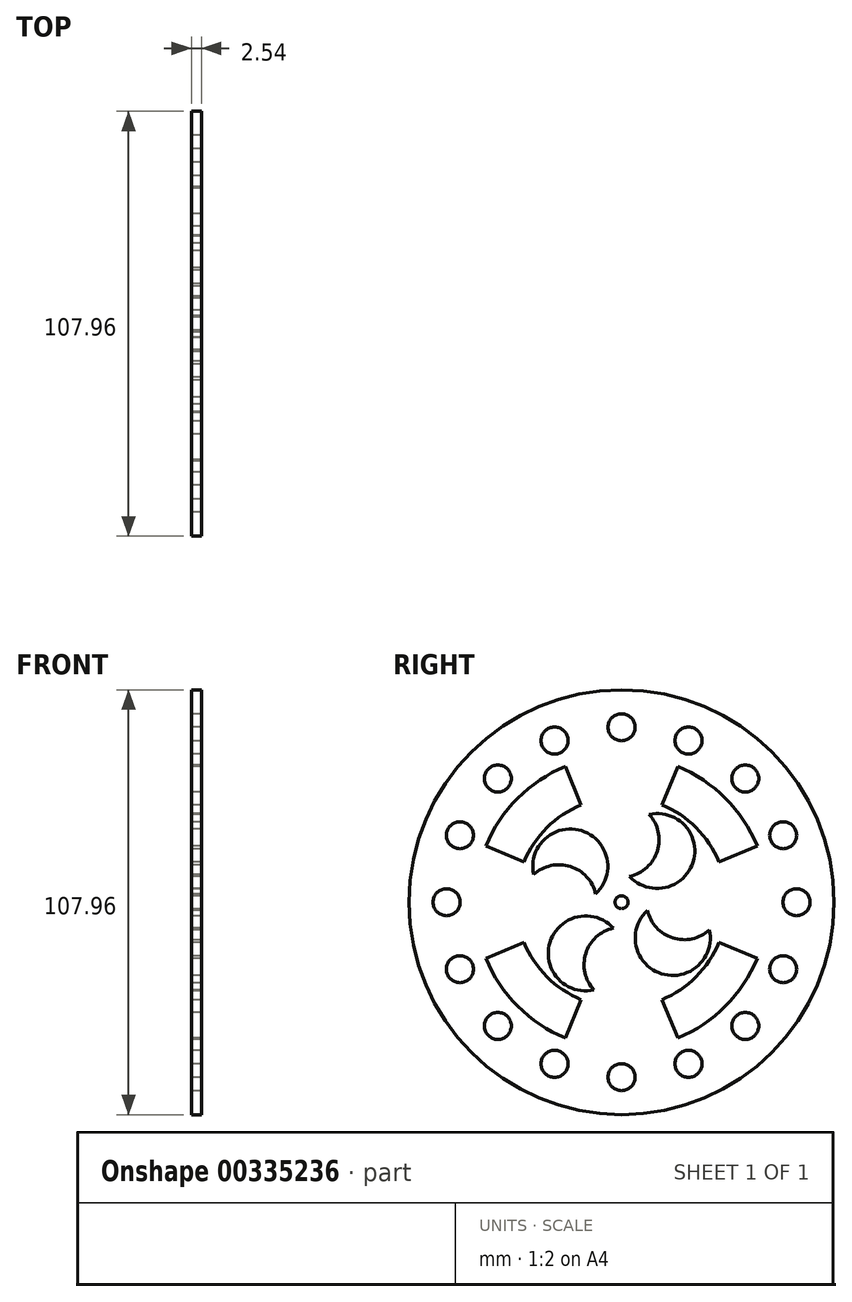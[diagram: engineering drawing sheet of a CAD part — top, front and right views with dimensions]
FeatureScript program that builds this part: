
annotation { "Feature Type Name" : "Feature", "Feature Type Description" : "" }
export const myFeature = defineFeature(function(context is Context, id is Id, definition is map)
    precondition{}
    {
        {
            var Q0;
            Q0=qCreatedBy(makeId("Right.planeOp"),FACE);
            var sketch = newSketch(context, id + "F0", { "sketchPlane" : qUnion([Q0])});
            skCircle(sketch, "E0", {"center": v(0, 0) * mm, "radius": 53.98 * mm});
            skCircle(sketch, "E1", {"center": v(0, 0) * mm, "radius": 1.65 * mm});
            skCircle(sketch, "E2", {"center": v(0, 44.45) * mm, "radius": 3.43 * mm});
            skCircle(sketch, "E3", {"center": v(-44.45, 0) * mm, "radius": 3.43 * mm});
            skLineSegment(sketch, "E4", {"start": v(-76.85, 0) * mm, "end": v(-47.88, 0) * mm, "construction": true});
            skArc(sketch, "E5", {"start": v(2.07, 6.58) * mm, "mid": v(9.09, 13.02) * mm, "end": v(7.02, 22.32) * mm});
            skArc(sketch, "E6", {"start": v(6.58, -2.07) * mm, "mid": v(13.02, -9.09) * mm, "end": v(22.32, -7.02) * mm});
            skArc(sketch, "E7", {"start": v(6.58, -2.07) * mm, "mid": v(10.16, -18.17) * mm, "end": v(22.32, -7.02) * mm});
            skArc(sketch, "E8.trimOffspring", {"start": v(-6.58, 2.07) * mm, "mid": v(-10.16, 18.17) * mm, "end": v(-22.32, 7.02) * mm});
            skArc(sketch, "E9.trimOffspring", {"start": v(-6.58, 2.07) * mm, "mid": v(-13.02, 9.09) * mm, "end": v(-22.32, 7.02) * mm});
            skArc(sketch, "E10.trimOffspring", {"start": v(-2.07, -6.58) * mm, "mid": v(-18.17, -10.16) * mm, "end": v(-7.02, -22.32) * mm});
            skArc(sketch, "E11.trimOffspring", {"start": v(-2.07, -6.58) * mm, "mid": v(-9.09, -13.02) * mm, "end": v(-7.02, -22.32) * mm});
            skArc(sketch, "E12.trimOffspring", {"start": v(2.07, 6.58) * mm, "mid": v(18.17, 10.16) * mm, "end": v(7.02, 22.32) * mm});
            skLineSegment(sketch, "E13.trimOffspring", {"start": v(-41.02, 0) * mm, "end": v(-1.65, 0) * mm, "construction": true});
            skCircle(sketch, "E14", {"center": v(-31.43, 31.43) * mm, "radius": 3.43 * mm});
            skPoint(sketch, "E15", {"position": v(-37.94, 15.72) * mm});
            skLineSegment(sketch, "E16", {"start": v(-1.53, 0.63) * mm, "end": v(-37.94, 15.72) * mm, "construction": true});
            skLineSegment(sketch, "E17", {"start": v(-37.94, 15.72) * mm, "end": v(-49.87, 20.66) * mm, "construction": true});
            skLineSegment(sketch, "E18", {"start": v(-0.63, 1.53) * mm, "end": v(-15.72, 37.94) * mm, "construction": true});
            skLineSegment(sketch, "E19", {"start": v(-15.72, 37.94) * mm, "end": v(-20.66, 49.87) * mm, "construction": true});
            skCircle(sketch, "E20", {"center": v(-41.07, 17.01) * mm, "radius": 3.43 * mm});
            skCircle(sketch, "E21", {"center": v(-17.01, 41.07) * mm, "radius": 3.43 * mm});
            skLineSegment(sketch, "E22", {"start": v(0, 71.42) * mm, "end": v(0, 1.65) * mm, "construction": true});
            skCircle(sketch, "E23.MirrorC", {"center": v(17.01, 41.07) * mm, "radius": 3.43 * mm});
            skCircle(sketch, "E24.MirrorC", {"center": v(31.43, 31.43) * mm, "radius": 3.43 * mm});
            skCircle(sketch, "E25.MirrorC", {"center": v(41.07, 17.01) * mm, "radius": 3.43 * mm});
            skCircle(sketch, "E26.MirrorC", {"center": v(44.45, 0) * mm, "radius": 3.43 * mm});
            skCircle(sketch, "E27.MirrorC", {"center": v(41.07, -17.01) * mm, "radius": 3.43 * mm});
            skCircle(sketch, "E28.MirrorC", {"center": v(31.43, -31.43) * mm, "radius": 3.43 * mm});
            skCircle(sketch, "E29.MirrorC", {"center": v(17.01, -41.07) * mm, "radius": 3.43 * mm});
            skCircle(sketch, "E30.MirrorC", {"center": v(0, -44.45) * mm, "radius": 3.43 * mm});
            skCircle(sketch, "E31.MirrorC", {"center": v(-17.01, -41.07) * mm, "radius": 3.43 * mm});
            skCircle(sketch, "E32.MirrorC", {"center": v(-31.43, -31.43) * mm, "radius": 3.43 * mm});
            skCircle(sketch, "E33.MirrorC", {"center": v(-41.07, -17.01) * mm, "radius": 3.43 * mm});
            skLineSegment(sketch, "E34.trimOffspring", {"start": v(0, -1.65) * mm, "end": v(0, -67.4) * mm, "construction": true});
            skLineSegment(sketch, "E35.trimOffspring", {"start": v(0, 0) * mm, "end": v(75.85, 0) * mm, "construction": true});
            skLineSegment(sketch, "E36.MirrorCS", {"start": v(0.63, 1.53) * mm, "end": v(15.72, 37.94) * mm, "construction": true});
            skLineSegment(sketch, "E37.MirrorCS", {"start": v(1.53, 0.63) * mm, "end": v(37.94, 15.72) * mm, "construction": true});
            skLineSegment(sketch, "E38.MirrorCS", {"start": v(-1.53, -0.63) * mm, "end": v(-37.94, -15.72) * mm, "construction": true});
            skLineSegment(sketch, "E39.MirrorCS", {"start": v(-0.63, -1.53) * mm, "end": v(-15.72, -37.94) * mm, "construction": true});
            skLineSegment(sketch, "E40.MirrorCS", {"start": v(1.53, -0.63) * mm, "end": v(37.94, -15.72) * mm, "construction": true});
            skLineSegment(sketch, "E41.MirrorCS", {"start": v(0.63, -1.53) * mm, "end": v(15.72, -37.94) * mm, "construction": true});
            skArc(sketch, "E42", {"start": v(-34.49, -14.29) * mm, "mid": v(-26.4, -26.4) * mm, "end": v(-14.29, -34.49) * mm});
            skArc(sketch, "E43", {"start": v(-24.76, -10.25) * mm, "mid": v(-18.95, -18.95) * mm, "end": v(-10.25, -24.76) * mm});
            skLineSegment(sketch, "E44", {"start": v(-24.76, -10.25) * mm, "end": v(-34.49, -14.29) * mm});
            skLineSegment(sketch, "E45", {"start": v(-10.25, -24.76) * mm, "end": v(-14.29, -34.49) * mm});
            skLineSegment(sketch, "E46", {"start": v(24.76, -10.25) * mm, "end": v(34.49, -14.29) * mm});
            skLineSegment(sketch, "E47", {"start": v(10.25, -24.76) * mm, "end": v(14.29, -34.49) * mm});
            skLineSegment(sketch, "E48", {"start": v(24.76, 10.25) * mm, "end": v(34.49, 14.29) * mm});
            skLineSegment(sketch, "E49", {"start": v(10.25, 24.76) * mm, "end": v(14.29, 34.49) * mm});
            skLineSegment(sketch, "E50", {"start": v(-14.29, 34.49) * mm, "end": v(-10.25, 24.76) * mm});
            skLineSegment(sketch, "E51", {"start": v(-34.49, 14.29) * mm, "end": v(-24.76, 10.25) * mm});
            skArc(sketch, "E52.trimOffspring", {"start": v(-14.29, 34.49) * mm, "mid": v(-26.4, 26.4) * mm, "end": v(-34.49, 14.29) * mm});
            skArc(sketch, "E53.trimOffspring", {"start": v(-10.25, 24.76) * mm, "mid": v(-18.95, 18.95) * mm, "end": v(-24.76, 10.25) * mm});
            skArc(sketch, "E54.trimOffspring", {"start": v(24.76, 10.25) * mm, "mid": v(18.95, 18.95) * mm, "end": v(10.25, 24.76) * mm});
            skArc(sketch, "E55.trimOffspring", {"start": v(34.49, 14.29) * mm, "mid": v(26.4, 26.4) * mm, "end": v(14.29, 34.49) * mm});
            skArc(sketch, "E56.trimOffspring", {"start": v(10.25, -24.76) * mm, "mid": v(18.95, -18.95) * mm, "end": v(24.76, -10.25) * mm});
            skArc(sketch, "E57.trimOffspring", {"start": v(14.29, -34.49) * mm, "mid": v(26.4, -26.4) * mm, "end": v(34.49, -14.29) * mm});
            skSolve(sketch);
        }
        {
            var Q0;
            Q0=makeQuery(id+"F0.imprint","IMPRINT",FACE,{"disambiguationData":[TD([[makeQuery(id+"F0.imprint","IMPRINT",EDGE,{"derivedFrom":sQuery(id+"F0.wireOp",EDGE,"E0")}),1.0]])]});
            extrude(context, id + "F1", {"entities" : qUnion([Q0]), "depth" : 2.54 * mm});
        }
    });
